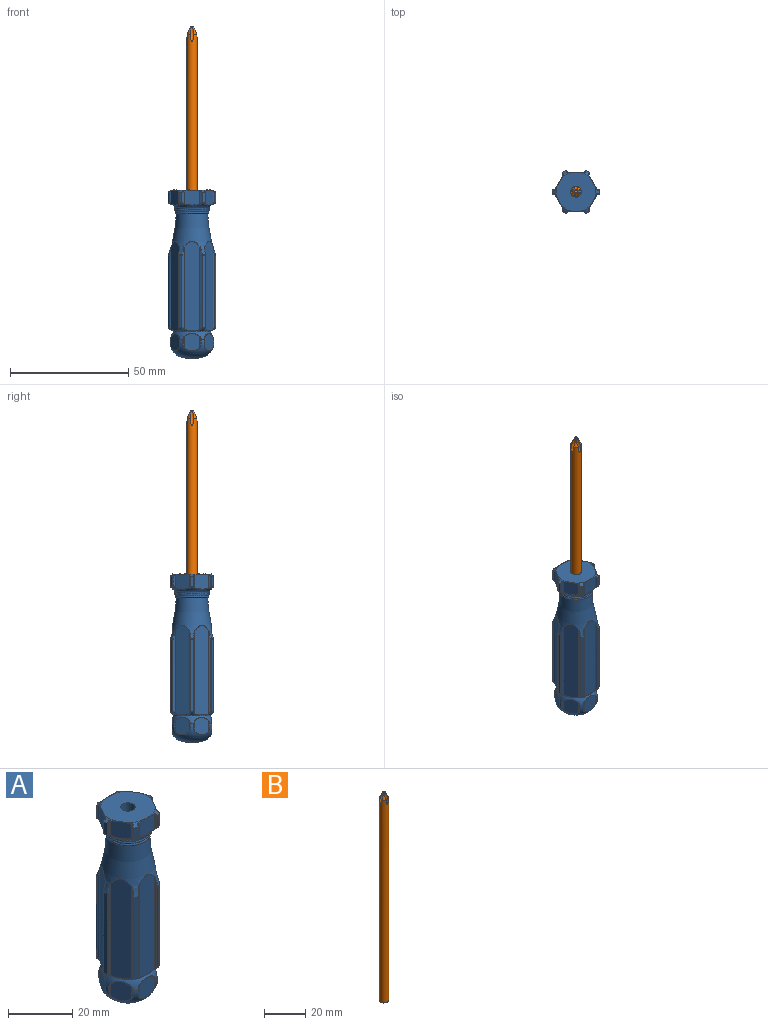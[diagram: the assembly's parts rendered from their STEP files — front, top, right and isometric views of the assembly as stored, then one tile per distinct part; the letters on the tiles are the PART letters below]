
ASSEMBLY  parts=2 mates=1
PART A: 346 faces, bbox 50.1x50.1x73.6 mm
  f0: torus R=7.41mm, axis (0,0,-1), area 9.4mm2, adj f13,f14
  f1: torus R=7mm, axis (0,0,-1), area 1.2mm2, adj f16,f17
  f2: torus R=6.75mm, axis (0,0,-1), area 1.3mm2, adj f19,f20
  f3: cone r=2.22mm half-angle=45deg, axis (0,0,1), area 0.4mm2, adj f4,f35
  f4: cylinder r=2.22mm len=53.32mm, axis (0,0,1), area 744.6mm2, adj f3,f345
  f5: cone r=8.46mm half-angle=60deg, axis (0,0,-1), area 3.5mm2, adj f35,f306,f307,f308,f309,f310,f337,f338
  f6: cylinder r=0.28mm len=4.26mm, axis (0,0,1), area 2.4mm2, adj f258,f259,f297,f298,f328
  f7: cylinder r=10mm len=4.26mm, axis (0,0,1), area 6.9mm2, adj f256,f294,f295,f323
  f8: cylinder r=0.28mm len=4.48mm, axis (0,0,1), area 2.4mm2, adj f253,f291,f292,f319
  f9: cylinder r=0.56mm len=5.44mm, axis (0,0,1), area 4.3mm2, adj f234,f235,f305,f335,f336
  f10: cylinder r=0.56mm len=5.44mm, axis (0,0,1), area 4.3mm2, adj f232,f233,f269,f340,f341
  f11: torus R=9.45mm, axis (0,0,-1), area 1.1mm2, adj f12,f230,f237,f267,f268,f308
  f12: torus R=11.11mm, axis (0,0,1), area 82.9mm2, adj f11,f13,f227,f228,f231,f232,f235,f236
  f13: torus R=7.4mm, axis (0,0,1), area 0.8mm2, adj f0,f12
  f14: torus R=6.91mm, axis (0,0,-1), area 36.3mm2, adj f0,f15
  f15: torus R=7.01mm, axis (0,0,1), area 0.8mm2, adj f14,f16
  f16: torus R=11.11mm, axis (0,0,1), area 1.4mm2, adj f1,f15
  f17: torus R=6.81mm, axis (0,0,-1), area 56.4mm2, adj f1,f18
  f18: torus R=6.75mm, axis (0,0,1), area 1.1mm2, adj f17,f19
  f19: torus R=11.11mm, axis (0,0,1), area 0.4mm2, adj f2,f18
  f20: torus R=6.72mm, axis (0,0,-1), area 62.3mm2, adj f2,f21
  f21: torus R=59.99mm, axis (0,0,1), area 633.5mm2, adj f20,f22,f203,f204,f205,f206,f207,f208
  f22: torus R=9.45mm, axis (0,0,-1), area 0.3mm2, adj f21,f176,f177,f178,f179,f180
  f23: cylinder r=10mm len=30.69mm, axis (0,0,1), area 49.5mm2, adj f155,f156,f157,f225
  f24: cylinder r=0.56mm len=34.86mm, axis (0,0,1), area 28.8mm2, adj f132,f133,f134,f182,f184,f216
  f25: cylinder r=0.56mm len=34.86mm, axis (0,0,1), area 28.8mm2, adj f119,f120,f121,f173,f174,f211
  f26: cylinder r=0.28mm len=30.69mm, axis (0,0,1), area 17.2mm2, adj f98,f147,f193,f194
  f27: torus R=9.45mm, axis (0,0,-1), area 0.9mm2, adj f29,f93,f94,f124,f129,f179
  f28: cylinder r=0.28mm len=30.69mm, axis (0,0,1), area 17.2mm2, adj f89,f106,f163,f164
  f29: cone r=7.78mm half-angle=60deg, axis (0,0,1), area 47.7mm2, adj f27,f30,f102,f103,f104,f108,f111,f112
  f30: cylinder r=7.78mm len=15.56mm, axis (0,0,1), area 8.7mm2, adj f29,f31
  f31: torus R=1.33mm, axis (0,0,1), area 92.6mm2, adj f30,f32,f71,f72,f73,f74,f75,f76
  f32: torus R=2.6mm, axis (0,0,1), area 306.6mm2, adj f31,f50,f51,f52,f53,f54,f55,f56
  f33: cylinder r=0.56mm len=4.37mm, axis (0,0,1), area 1.2mm2, adj f46,f53,f83
  f34: cylinder r=0.56mm len=4.37mm, axis (0,0,1), area 1.2mm2, adj f43,f58,f78
  f35: plane 16.92x16.45mm, normal (0,0,1), area 205.7mm2, adj f3,f5,f319,f323,f324,f328,f329,f333
  f36: cylinder r=0.56mm len=4.37mm, axis (0,0,1), area 5.4mm2, adj f65,f70,f71
  f37: cylinder r=0.56mm len=4.37mm, axis (0,0,1), area 1.6mm2, adj f38,f64,f72
  f38: plane 9.42x8mm, normal (0.87,-0.5,0), area 42.3mm2, adj f37,f39,f63,f73
  f39: cylinder r=0.56mm len=4.37mm, axis (0,0,1), area 5.4mm2, adj f38,f62,f74
  f40: cylinder r=0.56mm len=4.37mm, axis (0,0,1), area 1.6mm2, adj f41,f61,f75
  f41: plane 9.42x8.89mm, normal (0,-1,0), area 42.3mm2, adj f40,f42,f60,f76
  f42: cylinder r=0.56mm len=4.37mm, axis (0,0,1), area 5.4mm2, adj f41,f59,f77
  f43: plane 9.42x8mm, normal (-0.87,-0.5,0), area 42.3mm2, adj f34,f44,f57,f79
  f44: cylinder r=0.56mm len=4.37mm, axis (0,0,1), area 5.4mm2, adj f43,f56,f80
  f45: cylinder r=0.56mm len=4.37mm, axis (0,0,1), area 1.6mm2, adj f46,f55,f81
  f46: plane 9.42x8mm, normal (-0.87,0.5,0), area 42.3mm2, adj f33,f45,f54,f82
  f47: cylinder r=0.56mm len=4.37mm, axis (0,0,1), area 1.6mm2, adj f48,f52,f84
  f48: plane 9.42x8.89mm, normal (0,1,0), area 42.3mm2, adj f47,f49,f51,f85
  f49: cylinder r=0.56mm len=4.37mm, axis (0,0,1), area 5.4mm2, adj f48,f50,f86
  f50: bspline ~3.4x0.64mm, area 0.9mm2, adj f32,f49,f51,f86
  f51: bspline ~6.87x1.5mm, area 1.2mm2, adj f32,f48,f50,f52
  f52: bspline ~3.4x0.64mm, area 0.9mm2, adj f32,f47,f51,f84
  f53: bspline ~3.4x0.63mm, area 0.9mm2, adj f32,f33,f54,f83
  f54: bspline ~5.95x3.44mm, area 1.2mm2, adj f32,f46,f53,f55
  f55: bspline ~3.4x0.48mm, area 0.9mm2, adj f32,f45,f54,f81
  f56: bspline ~3.4x0.48mm, area 0.9mm2, adj f32,f44,f57,f80
  f57: bspline ~5.95x3.44mm, area 1.2mm2, adj f32,f43,f56,f58
  f58: bspline ~3.4x0.63mm, area 0.9mm2, adj f32,f34,f57,f78
  f59: bspline ~3.4x0.64mm, area 0.9mm2, adj f32,f42,f60,f77
  f60: bspline ~6.87x1.5mm, area 1.2mm2, adj f32,f41,f59,f61
  f61: bspline ~3.4x0.64mm, area 0.9mm2, adj f32,f40,f60,f75
  f62: bspline ~3.4x0.64mm, area 0.9mm2, adj f32,f39,f63,f74
  f63: bspline ~5.95x3.44mm, area 1.2mm2, adj f32,f38,f62,f64
  f64: bspline ~3.4x0.48mm, area 0.9mm2, adj f32,f37,f63,f72
  f65: bspline ~3.4x0.48mm, area 0.9mm2, adj f32,f36,f66,f71
  f66: bspline ~5.95x3.44mm, area 1.2mm2, adj f32,f65,f68,f70
  f67: plane 5.21x5.21mm, normal (0,0,-1), area 21.3mm2, adj f32
  f68: bspline ~3.4x0.63mm, area 0.9mm2, adj f32,f66,f69,f87
  f69: cylinder r=0.56mm len=4.37mm, axis (0,0,1), area 1.6mm2, adj f68,f70,f87
  f70: plane 9.42x8mm, normal (0.87,0.5,0), area 42.3mm2, adj f36,f66,f69,f88
  f71: bspline ~1.21x0.43mm, area 0.3mm2, adj f31,f36,f65,f88
  f72: bspline ~1.21x0.43mm, area 0.3mm2, adj f31,f37,f64,f73
  f73: bspline ~5.95x3.44mm, area 1.1mm2, adj f31,f38,f72,f74
  f74: bspline ~1.21x0.52mm, area 0.3mm2, adj f31,f39,f62,f73
  f75: bspline ~1.21x0.54mm, area 0.3mm2, adj f31,f40,f61,f76
  f76: bspline ~6.87x1.61mm, area 1.1mm2, adj f31,f41,f75,f77
  f77: bspline ~1.21x0.54mm, area 0.3mm2, adj f31,f42,f59,f76
  f78: bspline ~1.21x0.52mm, area 0.3mm2, adj f31,f34,f58,f79
  f79: bspline ~5.95x3.44mm, area 1.1mm2, adj f31,f43,f78,f80
  f80: bspline ~1.21x0.43mm, area 0.3mm2, adj f31,f44,f56,f79
  f81: bspline ~1.21x0.43mm, area 0.3mm2, adj f31,f45,f55,f82
  f82: bspline ~5.95x3.44mm, area 1.1mm2, adj f31,f46,f81,f83
  f83: bspline ~1.21x0.52mm, area 0.3mm2, adj f31,f33,f53,f82
  f84: bspline ~1.21x0.54mm, area 0.3mm2, adj f31,f47,f52,f85
  f85: bspline ~6.87x1.61mm, area 1.1mm2, adj f31,f48,f84,f86
  f86: bspline ~1.21x0.54mm, area 0.3mm2, adj f31,f49,f50,f85
  f87: bspline ~1.21x0.52mm, area 0.3mm2, adj f31,f68,f69,f88
  f88: bspline ~5.95x3.44mm, area 1.1mm2, adj f31,f70,f71,f87
  f89: bspline ~0.47x0.15mm, area 0.1mm2, adj f28,f105,f106,f108
  f90: bspline ~0.4x0.29mm, area 0.1mm2, adj f107,f108,f109,f110
  f91: bspline ~0.4x0.29mm, area 0.1mm2, adj f114,f115,f117,f118
  f92: bspline ~0.47x0.15mm, area 0.1mm2, adj f116,f118,f119,f120
  f93: bspline ~0.42x0.26mm, area 0.1mm2, adj f27,f124,f125,f127
  f94: bspline ~0.42x0.26mm, area 0.1mm2, adj f27,f126,f128,f129
  f95: bspline ~0.47x0.15mm, area 0.1mm2, adj f133,f134,f136,f137
  f96: bspline ~0.4x0.29mm, area 0.1mm2, adj f135,f137,f138,f139
  f97: bspline ~0.4x0.29mm, area 0.1mm2, adj f143,f144,f145,f146
  f98: bspline ~0.47x0.15mm, area 0.1mm2, adj f26,f146,f147,f148
  f99: bspline ~0.42x0.26mm, area 0.1mm2, adj f101,f153,f155,f157
  f100: bspline ~0.42x0.26mm, area 0.1mm2, adj f152,f154,f156,f157
  f101: bspline ~0.5x0.43mm, area 0.2mm2, adj f99,f102,f157,f158
  f102: bspline ~1.01x0.8mm, area 0.4mm2, adj f29,f101,f103,f158
  f103: bspline ~5.91x3.5mm, area 2mm2, adj f29,f102,f104,f159
  f104: bspline ~1.06x0.8mm, area 0.4mm2, adj f29,f103,f105,f160
  f105: bspline ~0.52x0.43mm, area 0.2mm2, adj f89,f104,f108,f160
  f106: plane 30.81x0.01mm, normal (0.5,0.87,0), area 0.2mm2, adj f28,f89,f160,f163
  f107: cylinder r=0.28mm len=30.69mm, axis (0,0,1), area 17.2mm2, adj f90,f109,f161,f164
  f108: torus R=9.45mm, axis (0,0,-1), area 0.9mm2, adj f29,f89,f90,f105,f110,f164
  f109: plane 30.81x0.01mm, normal (-1,0,0), area 0.2mm2, adj f90,f107,f161,f166
  f110: bspline ~0.43x0.4mm, area 0.2mm2, adj f90,f108,f111,f166
  f111: bspline ~0.88x0.8mm, area 0.4mm2, adj f29,f110,f112,f166
  f112: bspline ~6.78x0.63mm, area 2mm2, adj f29,f111,f113,f167
  f113: bspline ~0.88x0.8mm, area 0.4mm2, adj f29,f112,f114,f168
  f114: bspline ~0.43x0.4mm, area 0.2mm2, adj f91,f113,f118,f168
  f115: plane 30.81x0.01mm, normal (1,0,0), area 0.2mm2, adj f91,f117,f168,f171
  f116: cylinder r=0.28mm len=30.69mm, axis (0,0,1), area 17.2mm2, adj f92,f119,f169,f172
  f117: cylinder r=0.28mm len=30.69mm, axis (0,0,1), area 17.2mm2, adj f91,f115,f171,f172
  f118: torus R=9.45mm, axis (0,0,-1), area 0.9mm2, adj f29,f91,f92,f114,f120,f172
  f119: plane 30.81x0.01mm, normal (-0.5,0.87,0), area 0.2mm2, adj f25,f92,f116,f169
  f120: bspline ~0.52x0.43mm, area 0.2mm2, adj f25,f92,f118,f121
  f121: bspline ~1.06x0.8mm, area 0.4mm2, adj f25,f29,f120,f122
  f122: bspline ~5.91x3.5mm, area 2mm2, adj f29,f121,f123,f174
  f123: bspline ~1.01x0.8mm, area 0.4mm2, adj f29,f122,f124,f175
  f124: bspline ~0.5x0.43mm, area 0.2mm2, adj f27,f93,f123,f175
  f125: plane 30.81x0.01mm, normal (0.5,-0.87,0), area 0.2mm2, adj f93,f127,f175,f178
  f126: cylinder r=0.28mm len=30.69mm, axis (0,0,1), area 17.2mm2, adj f94,f128,f176,f179
  f127: cylinder r=0.28mm len=30.69mm, axis (0,0,1), area 17.2mm2, adj f93,f125,f178,f179
  f128: plane 30.81x0.01mm, normal (0.5,0.87,0), area 0.2mm2, adj f94,f126,f176,f181
  f129: bspline ~0.5x0.43mm, area 0.2mm2, adj f27,f94,f130,f181
  f130: bspline ~1.01x0.8mm, area 0.4mm2, adj f29,f129,f131,f181
  f131: bspline ~5.91x3.5mm, area 2mm2, adj f29,f130,f132,f182
  f132: bspline ~1.06x0.8mm, area 0.4mm2, adj f24,f29,f131,f133
  f133: bspline ~0.52x0.43mm, area 0.2mm2, adj f24,f95,f132,f137
  f134: plane 30.81x0.01mm, normal (-0.5,-0.87,0), area 0.2mm2, adj f24,f95,f136,f185
  f135: cylinder r=0.28mm len=30.69mm, axis (0,0,1), area 17.2mm2, adj f96,f138,f183,f186
  f136: cylinder r=0.28mm len=30.69mm, axis (0,0,1), area 17.2mm2, adj f95,f134,f185,f186
  f137: torus R=9.45mm, axis (0,0,-1), area 0.9mm2, adj f29,f95,f96,f133,f139,f186
  f138: plane 30.81x0.01mm, normal (1,0,0), area 0.2mm2, adj f96,f135,f183,f188
  f139: bspline ~0.43x0.4mm, area 0.2mm2, adj f96,f137,f140,f188
  f140: bspline ~0.88x0.8mm, area 0.4mm2, adj f29,f139,f141,f188
  f141: bspline ~6.78x0.63mm, area 2mm2, adj f29,f140,f142,f189
  f142: bspline ~0.88x0.8mm, area 0.4mm2, adj f29,f141,f143,f190
  f143: bspline ~0.43x0.4mm, area 0.2mm2, adj f97,f142,f146,f190
  f144: plane 30.81x0.01mm, normal (-1,0,0), area 0.2mm2, adj f97,f145,f190,f192
  f145: cylinder r=0.28mm len=30.69mm, axis (0,0,1), area 17.2mm2, adj f97,f144,f192,f193
  f146: torus R=9.45mm, axis (0,0,-1), area 0.9mm2, adj f29,f97,f98,f143,f148,f193
  f147: plane 30.81x0.01mm, normal (0.5,-0.87,0), area 0.2mm2, adj f26,f98,f194,f196
  f148: bspline ~0.52x0.43mm, area 0.2mm2, adj f98,f146,f149,f196
  f149: bspline ~1.06x0.8mm, area 0.4mm2, adj f29,f148,f150,f196
  f150: bspline ~5.91x3.5mm, area 2mm2, adj f29,f149,f151,f197
  f151: bspline ~1.01x0.8mm, area 0.4mm2, adj f29,f150,f152,f198
  f152: bspline ~0.5x0.43mm, area 0.2mm2, adj f100,f151,f157,f198
  f153: plane 30.81x0.01mm, normal (-0.5,-0.87,0), area 0.2mm2, adj f99,f155,f158,f199
  f154: plane 30.81x0.01mm, normal (-0.5,0.87,0), area 0.2mm2, adj f100,f156,f198,f202
  f155: cylinder r=0.28mm len=30.69mm, axis (0,0,1), area 17.2mm2, adj f23,f99,f153,f199
  f156: cylinder r=0.28mm len=30.69mm, axis (0,0,1), area 17.2mm2, adj f23,f100,f154,f202
  f157: torus R=9.45mm, axis (0,0,-1), area 0.9mm2, adj f23,f29,f99,f100,f101,f152
  f158: cylinder r=0.56mm len=34.86mm, axis (0,0,1), area 28.8mm2, adj f101,f102,f153,f159,f200,f203
  f159: plane 37.71x5.78mm, normal (0.87,-0.5,0), area 244.7mm2, adj f103,f158,f160,f204
  f160: cylinder r=0.56mm len=34.86mm, axis (0,0,1), area 28.8mm2, adj f104,f105,f106,f159,f162,f205
  f161: bspline ~0.4x0.29mm, area 0.1mm2, adj f107,f109,f165,f206
  f162: bspline ~0.47x0.15mm, area 0mm2, adj f160,f163,f205,f206
  f163: bspline ~0.47x0.15mm, area 0.1mm2, adj f28,f106,f162,f206
  f164: cylinder r=10mm len=30.69mm, axis (0,0,1), area 49.5mm2, adj f28,f107,f108,f206
  f165: bspline ~0.39x0.28mm, area 0mm2, adj f161,f166,f206,f207
  f166: cylinder r=0.56mm len=34.86mm, axis (0,0,1), area 28.8mm2, adj f109,f110,f111,f165,f167,f207
  f167: plane 37.71x6.67mm, normal (0,-1,0), area 244.7mm2, adj f112,f166,f168,f208
  f168: cylinder r=0.56mm len=34.86mm, axis (0,0,1), area 28.8mm2, adj f113,f114,f115,f167,f170,f209
  f169: bspline ~0.47x0.15mm, area 0.1mm2, adj f116,f119,f173,f210
  f170: bspline ~0.39x0.28mm, area 0mm2, adj f168,f171,f209,f210
  f171: bspline ~0.4x0.29mm, area 0.1mm2, adj f115,f117,f170,f210
  f172: cylinder r=10mm len=30.69mm, axis (0,0,1), area 49.5mm2, adj f116,f117,f118,f210
  f173: bspline ~0.47x0.15mm, area 0mm2, adj f25,f169,f210,f211
  f174: plane 37.71x5.78mm, normal (-0.87,-0.5,0), area 244.7mm2, adj f25,f122,f175,f212
  f175: cylinder r=0.56mm len=34.86mm, axis (0,0,1), area 28.8mm2, adj f123,f124,f125,f174,f177,f213
  f176: bspline ~0.42x0.26mm, area 0.1mm2, adj f22,f126,f128,f180
  f177: bspline ~0.42x0.26mm, area 0mm2, adj f22,f175,f178,f213
  f178: bspline ~0.42x0.26mm, area 0.1mm2, adj f22,f125,f127,f177
  f179: cylinder r=10mm len=30.69mm, axis (0,0,1), area 49.5mm2, adj f22,f27,f126,f127
  f180: bspline ~0.42x0.26mm, area 0mm2, adj f22,f176,f181,f214
  f181: cylinder r=0.56mm len=34.86mm, axis (0,0,1), area 28.8mm2, adj f128,f129,f130,f180,f182,f214
  f182: plane 37.71x5.78mm, normal (-0.87,0.5,0), area 244.7mm2, adj f24,f131,f181,f215
  f183: bspline ~0.4x0.29mm, area 0.1mm2, adj f135,f138,f187,f217
  f184: bspline ~0.47x0.15mm, area 0mm2, adj f24,f185,f216,f217
  f185: bspline ~0.47x0.15mm, area 0.1mm2, adj f134,f136,f184,f217
  f186: cylinder r=10mm len=30.69mm, axis (0,0,1), area 49.5mm2, adj f135,f136,f137,f217
  f187: bspline ~0.39x0.28mm, area 0mm2, adj f183,f188,f217,f218
  f188: cylinder r=0.56mm len=34.86mm, axis (0,0,1), area 28.8mm2, adj f138,f139,f140,f187,f189,f218
  f189: plane 37.71x6.67mm, normal (0,1,0), area 244.7mm2, adj f141,f188,f190,f219
  f190: cylinder r=0.56mm len=34.86mm, axis (0,0,1), area 28.8mm2, adj f142,f143,f144,f189,f191,f220
  f191: bspline ~0.39x0.28mm, area 0mm2, adj f190,f192,f220,f221
  f192: bspline ~0.4x0.29mm, area 0.1mm2, adj f144,f145,f191,f221
  f193: cylinder r=10mm len=30.69mm, axis (0,0,1), area 49.5mm2, adj f26,f145,f146,f221
  f194: bspline ~0.47x0.15mm, area 0.1mm2, adj f26,f147,f195,f221
  f195: bspline ~0.47x0.15mm, area 0mm2, adj f194,f196,f221,f222
  f196: cylinder r=0.56mm len=34.86mm, axis (0,0,1), area 28.8mm2, adj f147,f148,f149,f195,f197,f222
  f197: plane 37.71x5.78mm, normal (0.87,0.5,0), area 244.7mm2, adj f150,f196,f198,f223
  f198: cylinder r=0.56mm len=34.86mm, axis (0,0,1), area 28.8mm2, adj f151,f152,f154,f197,f201,f224
  f199: bspline ~0.42x0.26mm, area 0.1mm2, adj f153,f155,f200,f225
  f200: bspline ~0.42x0.26mm, area 0mm2, adj f158,f199,f203,f225
  f201: bspline ~0.42x0.26mm, area 0mm2, adj f198,f202,f224,f225
  f202: bspline ~0.42x0.26mm, area 0.1mm2, adj f154,f156,f201,f225
  f203: bspline ~3.34x1.15mm, area 1.2mm2, adj f21,f158,f200,f204
  f204: bspline ~5.95x3.44mm, area 0.8mm2, adj f21,f159,f203,f205
  f205: bspline ~3.34x1.21mm, area 1.2mm2, adj f21,f160,f162,f204
  f206: torus R=9.45mm, axis (0,0,-1), area 0.3mm2, adj f21,f161,f162,f163,f164,f165
  f207: bspline ~3.34x0.95mm, area 1.2mm2, adj f21,f165,f166,f208
  f208: bspline ~6.87x2.53mm, area 0.8mm2, adj f21,f167,f207,f209
  f209: bspline ~3.34x0.95mm, area 1.2mm2, adj f21,f168,f170,f208
  f210: torus R=9.45mm, axis (0,0,-1), area 0.3mm2, adj f21,f169,f170,f171,f172,f173
  f211: bspline ~3.35x1.21mm, area 1.2mm2, adj f21,f25,f173,f212
  f212: bspline ~5.95x3.44mm, area 0.8mm2, adj f21,f174,f211,f213
  f213: bspline ~3.34x1.15mm, area 1.2mm2, adj f21,f175,f177,f212
  f214: bspline ~3.34x1.15mm, area 1.2mm2, adj f21,f180,f181,f215
  f215: bspline ~5.95x3.44mm, area 0.8mm2, adj f21,f182,f214,f216
  f216: bspline ~3.35x1.21mm, area 1.2mm2, adj f21,f24,f184,f215
  f217: torus R=9.45mm, axis (0,0,-1), area 0.3mm2, adj f21,f183,f184,f185,f186,f187
  f218: bspline ~3.34x0.95mm, area 1.2mm2, adj f21,f187,f188,f219
  f219: bspline ~6.87x2.53mm, area 0.8mm2, adj f21,f189,f218,f220
  f220: bspline ~3.34x0.95mm, area 1.2mm2, adj f21,f190,f191,f219
  f221: torus R=9.45mm, axis (0,0,-1), area 0.3mm2, adj f21,f191,f192,f193,f194,f195
  f222: bspline ~3.34x1.21mm, area 1.2mm2, adj f21,f195,f196,f223
  f223: bspline ~5.95x3.44mm, area 0.8mm2, adj f21,f197,f222,f224
  f224: bspline ~3.34x1.15mm, area 1.2mm2, adj f21,f198,f201,f223
  f225: torus R=9.45mm, axis (0,0,-1), area 0.3mm2, adj f21,f23,f199,f200,f201,f202
  f226: bspline ~0.47x0.41mm, area 0.2mm2, adj f227,f271,f272,f274
  f227: bspline ~0.85x0.68mm, area 0.4mm2, adj f12,f226,f273,f274
  f228: bspline ~0.85x0.68mm, area 0.4mm2, adj f12,f229,f273,f275
  f229: bspline ~0.47x0.41mm, area 0.2mm2, adj f228,f251,f252,f275
  f230: bspline ~0.53x0.47mm, area 0.2mm2, adj f11,f231,f268,f277
  f231: bspline ~0.91x0.68mm, area 0.4mm2, adj f12,f230,f276,f277
  f232: bspline ~0.99x0.68mm, area 0.4mm2, adj f10,f12,f233,f276
  f233: bspline ~0.54x0.47mm, area 0.2mm2, adj f10,f232,f270,f271
  f234: bspline ~0.54x0.47mm, area 0.2mm2, adj f9,f235,f264,f265
  f235: bspline ~0.99x0.68mm, area 0.4mm2, adj f9,f12,f234,f278
  f236: bspline ~0.91x0.68mm, area 0.4mm2, adj f12,f237,f278,f279
  f237: bspline ~0.53x0.47mm, area 0.2mm2, adj f11,f236,f267,f279
  f238: bspline ~0.47x0.41mm, area 0.2mm2, adj f239,f260,f261,f281
  f239: bspline ~0.85x0.68mm, area 0.4mm2, adj f12,f238,f280,f281
  f240: bspline ~0.85x0.68mm, area 0.4mm2, adj f12,f241,f280,f282
  f241: bspline ~0.47x0.41mm, area 0.2mm2, adj f240,f263,f264,f282
  f242: bspline ~0.53x0.47mm, area 0.2mm2, adj f243,f256,f257,f284
  f243: bspline ~0.91x0.68mm, area 0.4mm2, adj f12,f242,f283,f284
  f244: bspline ~0.99x0.68mm, area 0.4mm2, adj f12,f245,f283,f285
  f245: bspline ~0.54x0.47mm, area 0.2mm2, adj f244,f259,f260,f285
  f246: bspline ~0.54x0.47mm, area 0.2mm2, adj f247,f252,f253,f287
  f247: bspline ~0.99x0.68mm, area 0.4mm2, adj f12,f246,f286,f287
  f248: bspline ~0.91x0.68mm, area 0.4mm2, adj f12,f249,f286,f288
  f249: bspline ~0.53x0.47mm, area 0.2mm2, adj f248,f255,f256,f288
  f250: plane 4.16x0.01mm, normal (-1,0,0), area 0mm2, adj f251,f275,f289,f290
  f251: bspline ~0.4x0.29mm, area 0.1mm2, adj f229,f250,f252,f290
  f252: torus R=9.45mm, axis (0,0,-1), area 1.1mm2, adj f12,f229,f246,f251,f253,f291
  f253: bspline ~0.47x0.15mm, area 0.1mm2, adj f8,f246,f252,f292
  f254: plane 4.16x0.01mm, normal (-0.5,0.87,0), area 0mm2, adj f255,f288,f293,f294
  f255: bspline ~0.42x0.26mm, area 0.1mm2, adj f249,f254,f256,f294
  f256: torus R=9.45mm, axis (0,0,-1), area 1.1mm2, adj f7,f12,f242,f249,f255,f257
  f257: bspline ~0.42x0.26mm, area 0.1mm2, adj f242,f256,f295,f296
  f258: plane 4.16x0.01mm, normal (0.5,0.87,0), area 0mm2, adj f6,f259,f285,f297
  f259: bspline ~0.47x0.15mm, area 0.1mm2, adj f6,f245,f258,f260
  f260: torus R=9.45mm, axis (0,0,-1), area 1.1mm2, adj f12,f238,f245,f259,f261,f298
  f261: bspline ~0.4x0.29mm, area 0.1mm2, adj f238,f260,f299,f300
  f262: plane 4.16x0.01mm, normal (1,0,0), area 0mm2, adj f263,f282,f301,f302
  f263: bspline ~0.4x0.29mm, area 0.1mm2, adj f241,f262,f264,f302
  f264: torus R=9.45mm, axis (0,0,-1), area 1.1mm2, adj f12,f234,f241,f263,f265,f303
  f265: bspline ~0.47x0.15mm, area 0.1mm2, adj f234,f264,f304,f305
  f266: plane 4.16x0.01mm, normal (0.5,-0.87,0), area 0mm2, adj f267,f279,f306,f307
  f267: bspline ~0.42x0.26mm, area 0.1mm2, adj f11,f237,f266,f307
  f268: bspline ~0.42x0.26mm, area 0.1mm2, adj f11,f230,f309,f310
  f269: plane 4.16x0.01mm, normal (-0.5,-0.87,0), area 0mm2, adj f10,f270,f311,f312
  f270: bspline ~0.47x0.15mm, area 0.1mm2, adj f233,f269,f271,f312
  f271: torus R=9.45mm, axis (0,0,-1), area 1.1mm2, adj f12,f226,f233,f270,f272,f313
  f272: bspline ~0.4x0.29mm, area 0.1mm2, adj f226,f271,f314,f315
  f273: bspline ~6.78x0.71mm, area 1.7mm2, adj f12,f227,f228,f317
  f274: cylinder r=0.56mm len=5.44mm, axis (0,0,1), area 4.2mm2, adj f226,f227,f315,f316,f317
  f275: cylinder r=0.56mm len=5.44mm, axis (0,0,1), area 4.2mm2, adj f228,f229,f250,f317,f318
  f276: bspline ~5.91x3.49mm, area 1.7mm2, adj f12,f231,f232,f340
  f277: cylinder r=0.56mm len=5.44mm, axis (0,0,1), area 4.2mm2, adj f230,f231,f310,f339,f340
  f278: bspline ~5.91x3.49mm, area 1.7mm2, adj f12,f235,f236,f336
  f279: cylinder r=0.56mm len=5.44mm, axis (0,0,1), area 4.2mm2, adj f236,f237,f266,f336,f337
  f280: bspline ~6.78x0.71mm, area 1.7mm2, adj f12,f239,f240,f331
  f281: cylinder r=0.56mm len=5.44mm, axis (0,0,1), area 4.2mm2, adj f238,f239,f300,f330,f331
  f282: cylinder r=0.56mm len=5.44mm, axis (0,0,1), area 4.2mm2, adj f240,f241,f262,f331,f332
  f283: bspline ~5.91x3.49mm, area 1.7mm2, adj f12,f243,f244,f326
  f284: cylinder r=0.56mm len=5.44mm, axis (0,0,1), area 4.2mm2, adj f242,f243,f296,f325,f326
  f285: cylinder r=0.56mm len=5.44mm, axis (0,0,1), area 4.2mm2, adj f244,f245,f258,f326,f327
  f286: bspline ~5.91x3.49mm, area 1.7mm2, adj f12,f247,f248,f321
  f287: cylinder r=0.56mm len=5.44mm, axis (0,0,1), area 4.2mm2, adj f246,f247,f292,f320,f321
  f288: cylinder r=0.56mm len=5.44mm, axis (0,0,1), area 4.2mm2, adj f248,f249,f254,f321,f322
  f289: bspline ~0.34x0.33mm, area 0.1mm2, adj f250,f290,f318,f319
  f290: cylinder r=0.28mm len=4.26mm, axis (0,0,1), area 2.4mm2, adj f250,f251,f289,f291,f319
  f291: cylinder r=10mm len=4.26mm, axis (0,0,1), area 6.9mm2, adj f8,f252,f290,f319
  f292: plane 4.98x0.63mm, normal (0.5,-0.87,0), area 0.1mm2, adj f8,f253,f287,f319,f320
  f293: bspline ~0.41x0.34mm, area 0.1mm2, adj f254,f294,f322,f323
  f294: cylinder r=0.28mm len=4.26mm, axis (0,0,1), area 2.4mm2, adj f7,f254,f255,f293,f323
  f295: cylinder r=0.28mm len=4.48mm, axis (0,0,1), area 2.4mm2, adj f7,f257,f296,f323
  f296: plane 4.98x0.63mm, normal (-0.5,-0.87,0), area 0.1mm2, adj f257,f284,f295,f323,f325
  f297: bspline ~0.43x0.34mm, area 0.1mm2, adj f6,f258,f327,f328
  f298: cylinder r=10mm len=4.26mm, axis (0,0,1), area 6.9mm2, adj f6,f260,f299,f328
  f299: cylinder r=0.28mm len=4.48mm, axis (0,0,1), area 2.4mm2, adj f261,f298,f300,f328
  f300: plane 4.98x0.7mm, normal (-1,0,0), area 0.1mm2, adj f261,f281,f299,f328,f330
  f301: bspline ~0.34x0.33mm, area 0.1mm2, adj f262,f302,f332,f333
  f302: cylinder r=0.28mm len=4.26mm, axis (0,0,1), area 2.4mm2, adj f262,f263,f301,f303,f333
  f303: cylinder r=10mm len=4.26mm, axis (0,0,1), area 6.9mm2, adj f264,f302,f304,f333
  f304: cylinder r=0.28mm len=4.48mm, axis (0,0,1), area 2.4mm2, adj f265,f303,f305,f333
  f305: plane 4.98x0.63mm, normal (-0.5,0.87,0), area 0.1mm2, adj f9,f265,f304,f333,f335
  f306: bspline ~0.41x0.34mm, area 0.1mm2, adj f5,f266,f307,f337
  f307: cylinder r=0.28mm len=4.26mm, axis (0,0,1), area 2.4mm2, adj f5,f266,f267,f306,f308
  f308: cylinder r=10mm len=4.26mm, axis (0,0,1), area 6.9mm2, adj f5,f11,f307,f309
  f309: cylinder r=0.28mm len=4.48mm, axis (0,0,1), area 2.4mm2, adj f5,f268,f308,f310
  f310: plane 4.98x0.63mm, normal (0.5,0.87,0), area 0.1mm2, adj f5,f268,f277,f309,f339
  f311: bspline ~0.43x0.34mm, area 0.1mm2, adj f269,f312,f341,f342
  f312: cylinder r=0.28mm len=4.26mm, axis (0,0,1), area 2.4mm2, adj f269,f270,f311,f313,f342
  f313: cylinder r=10mm len=4.26mm, axis (0,0,1), area 6.9mm2, adj f271,f312,f314,f342
  f314: cylinder r=0.28mm len=4.48mm, axis (0,0,1), area 2.4mm2, adj f272,f313,f315,f342
  f315: plane 4.98x0.7mm, normal (1,0,0), area 0.1mm2, adj f272,f274,f314,f316,f342
  f316: bspline ~0.9x0.88mm, area 0.3mm2, adj f274,f315,f342,f344
  f317: plane 6.69x6.35mm, normal (0,1,0), area 40.1mm2, adj f273,f274,f275,f344
  f318: bspline ~0.89x0.88mm, area 0.5mm2, adj f275,f289,f319,f344
  f319: cone r=8.46mm half-angle=60deg, axis (0,0,-1), area 3.5mm2, adj f8,f35,f289,f290,f291,f292,f318,f320
  f320: bspline ~1.15x0.88mm, area 0.3mm2, adj f287,f292,f319,f324
  f321: plane 6.35x5.8mm, normal (0.87,0.5,0), area 40.1mm2, adj f286,f287,f288,f324
  f322: bspline ~1.14x0.88mm, area 0.5mm2, adj f288,f293,f323,f324
  f323: cone r=8.46mm half-angle=60deg, axis (0,0,-1), area 3.5mm2, adj f7,f35,f293,f294,f295,f296,f322,f324
  f324: bspline ~5.91x3.5mm, area 1.1mm2, adj f35,f319,f320,f321,f322,f323
  f325: bspline ~1.15x0.88mm, area 0.3mm2, adj f284,f296,f323,f329
  f326: plane 6.35x5.8mm, normal (0.87,-0.5,0), area 40.1mm2, adj f283,f284,f285,f329
  f327: bspline ~1.14x0.88mm, area 0.5mm2, adj f285,f297,f328,f329
  f328: cone r=8.46mm half-angle=60deg, axis (0,0,-1), area 3.5mm2, adj f6,f35,f297,f298,f299,f300,f327,f329
  f329: bspline ~5.91x3.5mm, area 1.1mm2, adj f35,f323,f325,f326,f327,f328
  f330: bspline ~0.9x0.88mm, area 0.3mm2, adj f281,f300,f328,f334
  f331: plane 6.69x6.35mm, normal (0,-1,0), area 40.1mm2, adj f280,f281,f282,f334
  f332: bspline ~0.89x0.88mm, area 0.5mm2, adj f282,f301,f333,f334
  f333: cone r=8.46mm half-angle=60deg, axis (0,0,-1), area 3.5mm2, adj f35,f301,f302,f303,f304,f305,f332,f334
  f334: bspline ~6.78x0.63mm, area 1.1mm2, adj f35,f328,f330,f331,f332,f333
  f335: bspline ~1.15x0.88mm, area 0.3mm2, adj f9,f305,f333,f338
  f336: plane 6.35x5.8mm, normal (-0.87,-0.5,0), area 40.1mm2, adj f9,f278,f279,f338
  f337: bspline ~1.14x0.88mm, area 0.5mm2, adj f5,f279,f306,f338
  f338: bspline ~5.91x3.5mm, area 1.1mm2, adj f5,f35,f333,f335,f336,f337
  f339: bspline ~1.15x0.88mm, area 0.3mm2, adj f5,f277,f310,f343
  f340: plane 6.35x5.8mm, normal (-0.87,0.5,0), area 40.1mm2, adj f10,f276,f277,f343
  f341: bspline ~1.14x0.88mm, area 0.5mm2, adj f10,f311,f342,f343
  f342: cone r=8.46mm half-angle=60deg, axis (0,0,-1), area 3.5mm2, adj f35,f311,f312,f313,f314,f315,f316,f341
  f343: bspline ~5.91x3.5mm, area 1.1mm2, adj f5,f35,f339,f340,f341,f342
  f344: bspline ~6.78x0.63mm, area 1.1mm2, adj f35,f316,f317,f318,f319,f342
  f345: plane 4.45x4.45mm, normal (0,0,1), area 15.5mm2, adj f4
PART B: 12 faces, bbox 5.2x5.2x123.6 mm
  f0: revolved ~6.39x2mm, area 13.6mm2, adj f4,f5,f6,f7
  f1: revolved ~6.39x2mm, area 13.6mm2, adj f4,f5,f7,f8
  f2: revolved ~6.39x2mm, area 13.6mm2, adj f4,f5,f8,f9
  f3: revolved ~6.39x2mm, area 13.6mm2, adj f4,f5,f6,f9
  f4: cone r=2.22mm half-angle=25.1deg, axis (0,0,-1), area 16.9mm2, adj f0,f1,f2,f3,f6,f7,f8,f9
  f5: cylinder r=2.22mm len=119.89mm, axis (0,0,1), area 1660.7mm2, adj f0,f1,f2,f3,f6,f7,f8,f9
  f6: torus R=1.67mm, axis (0,0,-1), area 0.5mm2, adj f0,f3,f4,f5
  f7: torus R=1.67mm, axis (0,0,-1), area 0.5mm2, adj f0,f1,f4,f5
  f8: torus R=1.67mm, axis (0,0,-1), area 0.5mm2, adj f1,f2,f4,f5
  f9: torus R=1.67mm, axis (0,0,-1), area 0.5mm2, adj f2,f3,f4,f5
  f10: plane 1.11x1.11mm, normal (0,0,1), area 1mm2, adj f4
  f11: plane 4.45x4.45mm, normal (0,0,-1), area 15.5mm2, adj f5
PLACE A at identity
PLACE B t=(0,0,-0.78)mm
MATE fastened B.f4 <-> A.f0  axis (0,0,-1) through (0,0,17)mm
